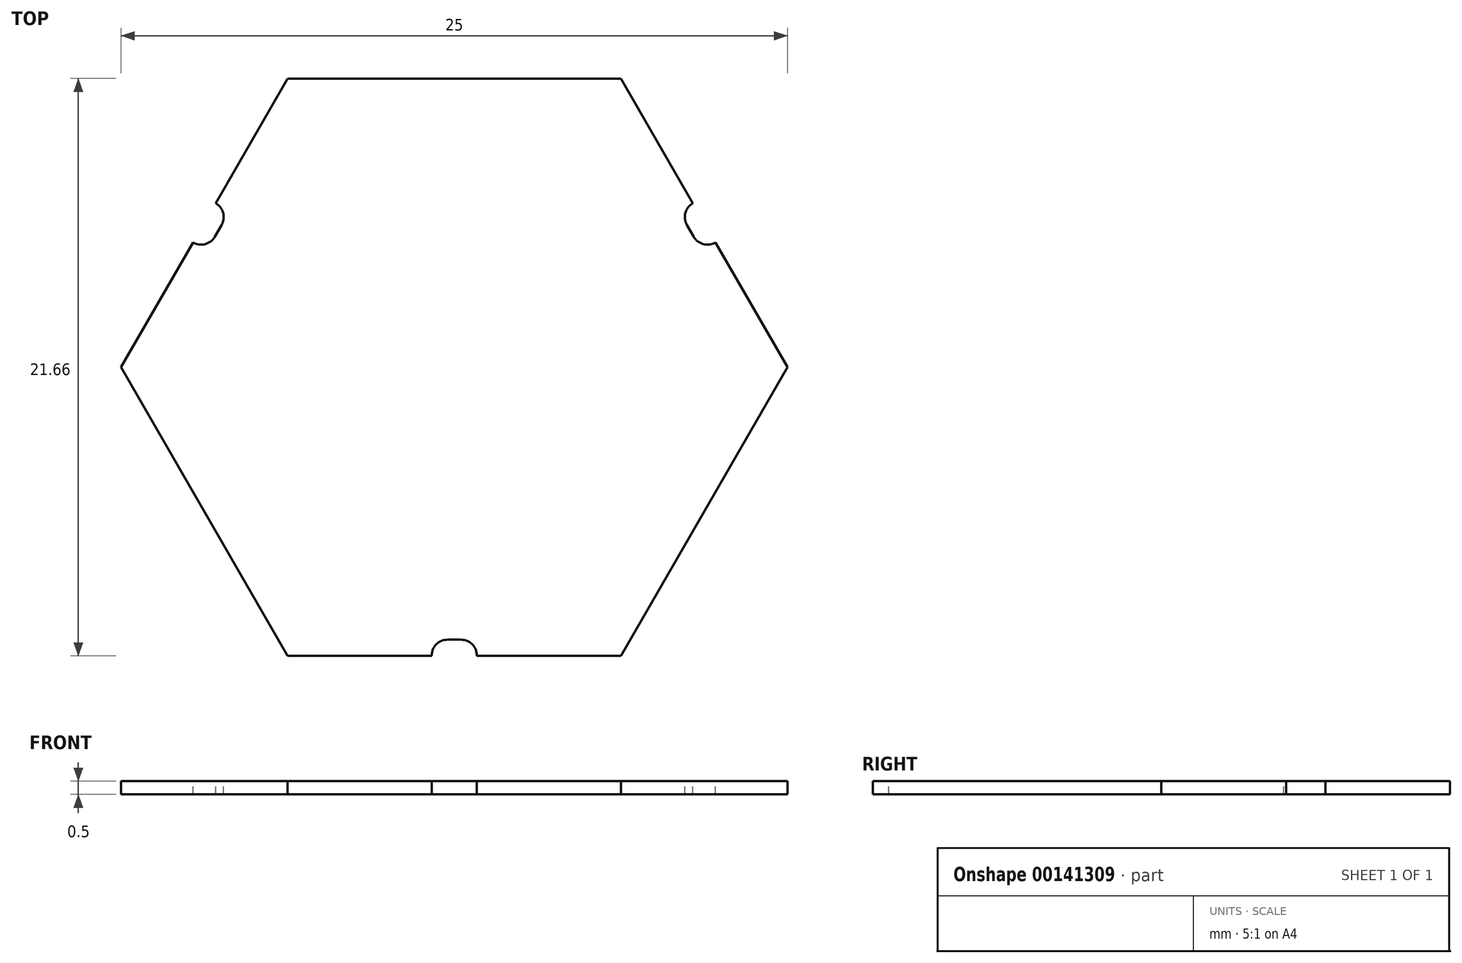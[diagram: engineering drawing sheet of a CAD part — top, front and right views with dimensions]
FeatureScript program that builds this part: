
annotation { "Feature Type Name" : "Feature", "Feature Type Description" : "" }
export const myFeature = defineFeature(function(context is Context, id is Id, definition is map)
    precondition{}
    {
        {
            var Q0;
            Q0=qCreatedBy(makeId("Top.planeOp"),FACE);
            var sketch = newSketch(context, id + "F0", { "sketchPlane" : qUnion([Q0])});
            skCircle(sketch, "E0.cCircle", {"center": v(0, 0) * mm, "radius": 12.5 * mm, "construction": true});
            skLineSegment(sketch, "E0.0", {"start": v(12.5, 0) * mm, "end": v(6.25, -10.83) * mm});
            skLineSegment(sketch, "E0.1", {"start": v(6.25, -10.83) * mm, "end": v(-6.25, -10.83) * mm});
            skLineSegment(sketch, "E0.2", {"start": v(-6.25, -10.83) * mm, "end": v(-12.5, 0) * mm});
            skLineSegment(sketch, "E0.3", {"start": v(-12.5, 0) * mm, "end": v(-6.25, 10.83) * mm});
            skLineSegment(sketch, "E0.4", {"start": v(-6.25, 10.83) * mm, "end": v(6.25, 10.83) * mm});
            skLineSegment(sketch, "E0.5", {"start": v(6.25, 10.83) * mm, "end": v(12.5, 0) * mm});
            skSolve(sketch);
        }
        {
            var Q0;
            Q0=qSketchRegion(id+"F0",true);
            extrude(context, id + "F1", {"entities" : qUnion([Q0]), "depth" : 0.5 * mm});
        }
        {
            var Q0;
            Q0=makeQuery(id+"F1.opExtrude","CAP_FACE",FACE,{"disambiguationData":[OSD([sQuery(id+"F0.wireOp",EDGE,"E0.0"),sQuery(id+"F0.wireOp",EDGE,"E0.1"),sQuery(id+"F0.wireOp",EDGE,"E0.2"),sQuery(id+"F0.wireOp",EDGE,"E0.3"),sQuery(id+"F0.wireOp",EDGE,"E0.4"),sQuery(id+"F0.wireOp",EDGE,"E0.5")])],"isStart":false});
            var sketch = newSketch(context, id + "F2", { "sketchPlane" : qUnion([Q0])});
            skLineSegment(sketch, "E1.0", {"start": v(6.25, -10.83) * mm, "end": v(-6.25, -10.83) * mm, "construction": true});
            skLineSegment(sketch, "E2", {"start": v(0.25, -10.23) * mm, "end": v(-0.25, -10.23) * mm});
            skArc(sketch, "E3", {"start": v(-0.25, -10.23) * mm, "mid": v(-0.67, -10.4) * mm, "end": v(-0.85, -10.83) * mm});
            skArc(sketch, "E4", {"start": v(0.85, -10.83) * mm, "mid": v(0.67, -10.4) * mm, "end": v(0.25, -10.23) * mm});
            skLineSegment(sketch, "E5", {"start": v(-0.85, -10.83) * mm, "end": v(0.85, -10.83) * mm});
            skArc(sketch, "E6.1.0", {"start": v(8.98, 4.9) * mm, "mid": v(9.34, 4.62) * mm, "end": v(9.8, 4.68) * mm});
            skLineSegment(sketch, "E6.1.1", {"start": v(9.8, 4.68) * mm, "end": v(8.95, 6.15) * mm});
            skLineSegment(sketch, "E6.1.2", {"start": v(8.73, 5.33) * mm, "end": v(8.98, 4.9) * mm});
            skArc(sketch, "E6.1.3", {"start": v(8.95, 6.15) * mm, "mid": v(8.67, 5.78) * mm, "end": v(8.73, 5.33) * mm});
            skArc(sketch, "E6.2.0", {"start": v(-8.73, 5.33) * mm, "mid": v(-8.67, 5.78) * mm, "end": v(-8.95, 6.15) * mm});
            skLineSegment(sketch, "E6.2.1", {"start": v(-8.95, 6.15) * mm, "end": v(-9.8, 4.68) * mm});
            skLineSegment(sketch, "E6.2.2", {"start": v(-8.98, 4.9) * mm, "end": v(-8.73, 5.33) * mm});
            skArc(sketch, "E6.2.3", {"start": v(-9.8, 4.68) * mm, "mid": v(-9.34, 4.62) * mm, "end": v(-8.98, 4.9) * mm});
            skPoint(sketch, "E6.center", {"position": v(0, 0) * mm});
            skSolve(sketch);
        }
        {
            var Q0;
            Q0 = qSketchRegion(id + "F2", true);
            extrude(context, id + "F3", {"entities" : qUnion([Q0]), "operationType" : NewBodyOperationType.REMOVE, "endBound" : BoundingType.THROUGH_ALL, "oppositeDirection" : true, "depth" : 25 * mm});
        }
    });
